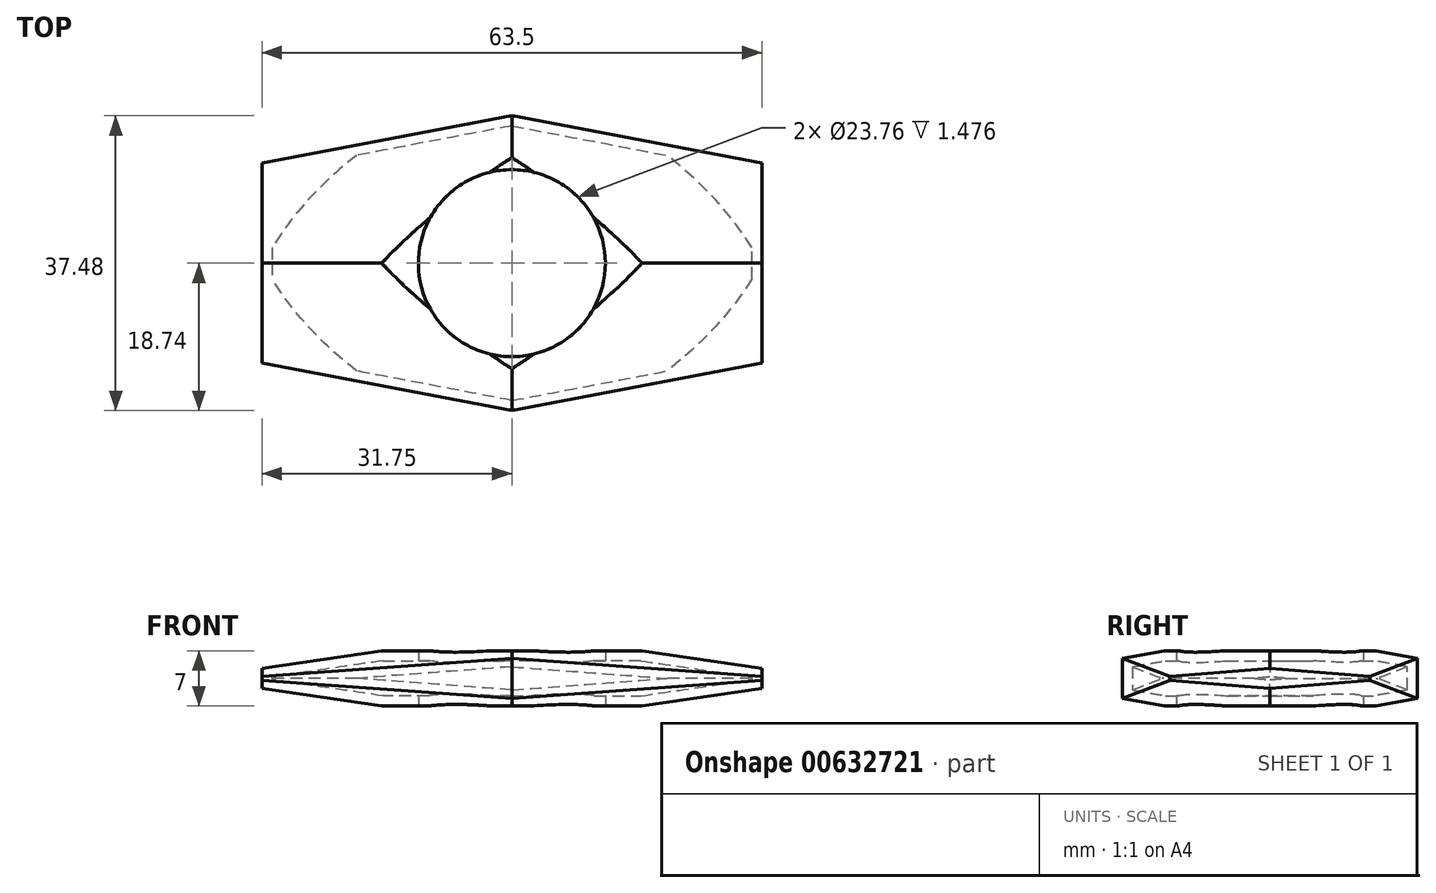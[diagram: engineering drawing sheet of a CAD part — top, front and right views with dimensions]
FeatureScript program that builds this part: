
annotation { "Feature Type Name" : "Feature", "Feature Type Description" : "" }
export const myFeature = defineFeature(function(context is Context, id is Id, definition is map)
    precondition{}
    {
        {
            var Q0;
            Q0=qCreatedBy(makeId("Right.planeOp"),FACE);
            var sketch = newSketch(context, id + "F0", { "sketchPlane" : qUnion([Q0])});
            skLineSegment(sketch, "E0", {"start": v(-18.74, 0) * mm, "end": v(-18.74, 2.54) * mm});
            skLineSegment(sketch, "E1", {"start": v(18.74, 0) * mm, "end": v(18.74, 2.54) * mm});
            skPoint(sketch, "E2", {"position": v(-11.88, 0) * mm});
            skPoint(sketch, "E3", {"position": v(11.88, 0) * mm});
            skLineSegment(sketch, "E4.MirrorCS", {"start": v(-18.74, 0) * mm, "end": v(-18.74, -2.54) * mm});
            skLineSegment(sketch, "E5.MirrorCS", {"start": v(18.74, 0) * mm, "end": v(18.74, -2.54) * mm});
            skPoint(sketch, "E6", {"position": v(0, 5.93) * mm});
            skPoint(sketch, "E7", {"position": v(0, -5.93) * mm});
            skLineSegment(sketch, "E8", {"start": v(-18.74, 2.54) * mm, "end": v(0, 5.93) * mm});
            skLineSegment(sketch, "E9", {"start": v(0, 5.93) * mm, "end": v(18.74, 2.54) * mm});
            skLineSegment(sketch, "E10", {"start": v(18.74, -2.54) * mm, "end": v(0, -5.93) * mm});
            skLineSegment(sketch, "E11", {"start": v(0, -5.93) * mm, "end": v(-18.74, -2.54) * mm});
            skSolve(sketch);
        }
        {
            var Q0;
            Q0=qCreatedBy(makeId("Right.planeOp"),FACE);
            cPlane(context, id + "F1", {"entities" : qUnion([Q0]), "cplaneType" : CPlaneType.OFFSET, "offset" : 31.75 * mm, "width" : 152.4 * mm, "height" : 152.4 * mm});
        }
        {
            var Q0;
            Q0=qCreatedBy(id+"F1.planeOp",FACE);
            var sketch = newSketch(context, id + "F2", { "sketchPlane" : qUnion([Q0])});
            skLineSegment(sketch, "E12", {"start": v(-12.7, 0) * mm, "end": v(-12.7, 0.25) * mm});
            skLineSegment(sketch, "E13", {"start": v(12.7, 0) * mm, "end": v(12.7, 0.25) * mm});
            skLineSegment(sketch, "E14.MirrorCS", {"start": v(-12.7, 0) * mm, "end": v(-12.7, -0.25) * mm});
            skLineSegment(sketch, "E15.MirrorCS", {"start": v(12.7, 0) * mm, "end": v(12.7, -0.25) * mm});
            skLineSegment(sketch, "E16", {"start": v(0, 1.27) * mm, "end": v(-12.7, 0.25) * mm});
            skLineSegment(sketch, "E17", {"start": v(0, 1.27) * mm, "end": v(12.7, 0.25) * mm});
            skLineSegment(sketch, "E18", {"start": v(12.7, -0.25) * mm, "end": v(0, -1.27) * mm});
            skLineSegment(sketch, "E19", {"start": v(0, -1.27) * mm, "end": v(-12.7, -0.25) * mm});
            skSolve(sketch);
        }
        {
            var Q0;
            Q0=makeQuery(id+"F0.imprint","IMPRINT",FACE,{"disambiguationData":[TD([[makeQuery(id+"F0.imprint","IMPRINT",EDGE,{"derivedFrom":sQuery(id+"F0.wireOp",EDGE,"E0")}),-1.0]])]});
            var Q1;
            Q1=makeQuery(id+"F2.imprint","IMPRINT",FACE,{"disambiguationData":[TD([[makeQuery(id+"F2.imprint","IMPRINT",EDGE,{"derivedFrom":sQuery(id+"F2.wireOp",EDGE,"E12")}),-1.0]])]});
            loft(context, id + "F3", {"sheetProfilesArray" : [{ "sheetProfileEntities" : qUnion([Q0]) }, { "sheetProfileEntities" : qUnion([Q1]) }]});
        }
        {
            var Q0;
            Q0=qCreatedBy(makeId("Right.planeOp"),FACE);
            cPlane(context, id + "F4", {"entities" : qUnion([Q0]), "cplaneType" : CPlaneType.OFFSET, "offset" : 31.75 * mm, "oppositeDirection" : true, "width" : 152.4 * mm, "height" : 152.4 * mm});
        }
        {
            var Q0;
            Q0=qCreatedBy(id+"F4.planeOp",FACE);
            var sketch = newSketch(context, id + "F5", { "sketchPlane" : qUnion([Q0])});
            skLineSegment(sketch, "E20", {"start": v(-12.7, 0) * mm, "end": v(-12.7, 0.25) * mm});
            skLineSegment(sketch, "E21.MirrorCS", {"start": v(-12.7, 0) * mm, "end": v(-12.7, -0.25) * mm});
            skLineSegment(sketch, "E22", {"start": v(0, 1.27) * mm, "end": v(-12.7, 0.25) * mm});
            skLineSegment(sketch, "E23", {"start": v(0, -1.27) * mm, "end": v(-12.7, -0.25) * mm});
            skLineSegment(sketch, "E24", {"start": v(0, 0) * mm, "end": v(0, -1.27) * mm});
            skLineSegment(sketch, "E25.MirrorCS", {"start": v(0, -1.27) * mm, "end": v(12.7, -0.25) * mm});
            skLineSegment(sketch, "E26.MirrorCS", {"start": v(12.7, 0) * mm, "end": v(12.7, -0.25) * mm});
            skLineSegment(sketch, "E27.MirrorCS", {"start": v(12.7, 0) * mm, "end": v(12.7, 0.25) * mm});
            skLineSegment(sketch, "E28.MirrorCS", {"start": v(0, 1.27) * mm, "end": v(12.7, 0.25) * mm});
            skSolve(sketch);
        }
        {
            var Q1;
            Q1 = qSketchRegion(id + "F0", true);
            var Q2;
            Q2=makeQuery(id+"F5.imprint","IMPRINT",FACE,{"disambiguationData":[TD([[makeQuery(id+"F5.imprint","IMPRINT",EDGE,{"derivedFrom":sQuery(id+"F5.wireOp",EDGE,"E20")}),-1.0]])]});
            loft(context, id + "F6", {"operationType" : NewBodyOperationType.ADD, "sheetProfilesArray" : [{ "sheetProfileEntities" : qUnion([Q1]) }, { "sheetProfileEntities" : qUnion([Q2]) }]});
        }
        {
            var Q0;
            Q0=qCreatedBy(makeId("Top.planeOp"),FACE);
            var sketch = newSketch(context, id + "F7", { "sketchPlane" : qUnion([Q0])});
            skCircle(sketch, "E29", {"center": v(0, 0) * mm, "radius": 11.88 * mm});
            skSolve(sketch);
        }
        {
            var Q0;
            Q0 = qSketchRegion(id + "F7", true);
            extrude(context, id + "F8", {"entities" : qUnion([Q0]), "operationType" : NewBodyOperationType.REMOVE, "endBound" : BoundingType.SYMMETRIC, "depth" : 25.4 * mm, "offsetDistance" : 25.4 * mm});
        }
        {
            var Q0;
            Q0=qCreatedBy(makeId("Right.planeOp"),FACE);
            var sketch = newSketch(context, id + "F9", { "sketchPlane" : qUnion([Q0])});
            skLineSegment(sketch, "E30.bottom", {"start": v(-27.28, 3.5) * mm, "end": v(27.28, 3.5) * mm});
            skLineSegment(sketch, "E30.top", {"start": v(-27.28, -3.5) * mm, "end": v(27.28, -3.5) * mm});
            skLineSegment(sketch, "E30.left", {"start": v(-27.28, 3.5) * mm, "end": v(-27.28, -3.5) * mm});
            skLineSegment(sketch, "E30.right", {"start": v(27.28, 3.5) * mm, "end": v(27.28, -3.5) * mm});
            skPoint(sketch, "E30.middle", {"position": v(0, 0) * mm});
            skLineSegment(sketch, "E31.bottom", {"start": v(32.43, 8.96) * mm, "end": v(-32.43, 8.96) * mm});
            skLineSegment(sketch, "E31.top", {"start": v(32.43, -8.96) * mm, "end": v(-32.43, -8.96) * mm});
            skLineSegment(sketch, "E31.left", {"start": v(32.43, 8.96) * mm, "end": v(32.43, -8.96) * mm});
            skLineSegment(sketch, "E31.right", {"start": v(-32.43, 8.96) * mm, "end": v(-32.43, -8.96) * mm});
            skSolve(sketch);
        }
        {
            var Q0;
            Q0=makeQuery(id+"F9.imprint","IMPRINT",FACE,{"disambiguationData":[TD([[makeQuery(id+"F9.imprint","IMPRINT",EDGE,{"derivedFrom":sQuery(id+"F9.wireOp",EDGE,"E30.bottom")}),1.0]])]});
            extrude(context, id + "F10", {"entities" : qUnion([Q0]), "operationType" : NewBodyOperationType.REMOVE, "endBound" : BoundingType.SYMMETRIC, "oppositeDirection" : true, "depth" : 76.2 * mm, "offsetDistance" : 25.4 * mm});
        }
        {
            var Q0;
            Q0=makeQuery(id+"F8.boolean.opBoolean","COPY",FACE,{"derivedFrom":makeQuery(id+"F8.opExtrude","SWEPT_FACE",FACE,{"disambiguationData":[OSD([sQuery(id+"F7.wireOp",EDGE,"E29")])]})});
            shell(context, id + "F11", {"entities" : qUnion([Q0]), "thickness" : 1.27 * mm});
        }
    });
